# Revit family: PlumbingFixture_Valve_AVG_TVA20CHP-i
name_source: partatom
category: Pipe Accessories
revit_build: Autodesk Revit 2017 (Build: 20190508_0315(x64)
units: mm (PartAtom-declared; Revit-internal decimal feet)

## family parameters
Always vertical = Yes
Cut with Voids When Loaded = No
OmniClass Number = 23.60.30.11.14
OmniClass Title = Pipework Fittings
Part Type = Valve - Breaks Into
Round Connector Dimension = Use Radius
Shared = No
Work Plane-Based = No

## types (1)
- Type 1
    Adjustable_Mixed-Outlet_Temp (°C ) = 40-50
    Bypass_Size = 0 mm  [stored 0 ft]
    CW Connection = No
    CWFU = 0
    Cold_Water_Supply_Temp (°C ) = 5-25
    Comments_For_Revit = Same valve design. HP Valve has an orange cap. The standard has a yellow cap. Same basic Valve (TMV20 & TVA20)
    Default Elevation = 0 mm  [stored 0 ft]
    Description = Tempering Valve Assembly HP-High Performance, with insulation. Suitable for solar and continous flow water heaters
    Factory_Set_Mixed_Temp (°C ) = 50
    HW Connection = No
    HWFU = 0
    Hot_Water_Supply_Temp (°C ) = 65-99
    Inlet_Size_CW = 20 mm  [stored 0.0656168 ft]
    Inlet_Size_CW Radius = 10 mm  [stored 0.0328084 ft]
    Inlet_Size_HW = 20 mm  [stored 0.0656168 ft]
    Inlet_Size_HW Radius = 10 mm  [stored 0.0328084 ft]
    Inlet_Type = Compression
    Loss Method = Not Defined
    Manufacturer = Australian Valve Group
    Max_Flow_Rate (l/min) = 27
    Max_Supply_Pressure_Dynamic (kPa) = 500
    Max_Supply_Pressure_Static (kPa) = 1400
    Min_Supply_Pressure_Dynamic (kPa) = 20
    Min_Supply_Pressure_Imbalance (%) = 10
    Min_Temp_Differential_Cold_to_Mixed (°C ) = 5
    Min_Temp_Differential_Hot_to_Mixed (°C ) = 10
    Minimum_Flow_Rate (l/min) = 4
    Outlet_Size = 20 mm  [stored 0.0656168 ft]
    Outlet_Size Radius = 10 mm  [stored 0.0328084 ft]
    Outlet_Type = Compression
    PlumbingMaterial_ANZRS = <By Category>
    Product_Type = TVA20CHP-i
    Specify_Host = Face
    Tolerance_Mixed-Outlet_Temp (°C ) = ±3
    URL = https://www.avg.net.au
    Valve_Model = TVA20C-i
    Vent Connection = No
    WFU = 0
    Waste Connection = No

note: [stored X ft] marks values corroborated as IEEE doubles in the binary element streams (Revit-internal decimal feet)

## geometry (parser evidence)
native form markers: Sweep x7
no freeform markers — native parametric forms only
